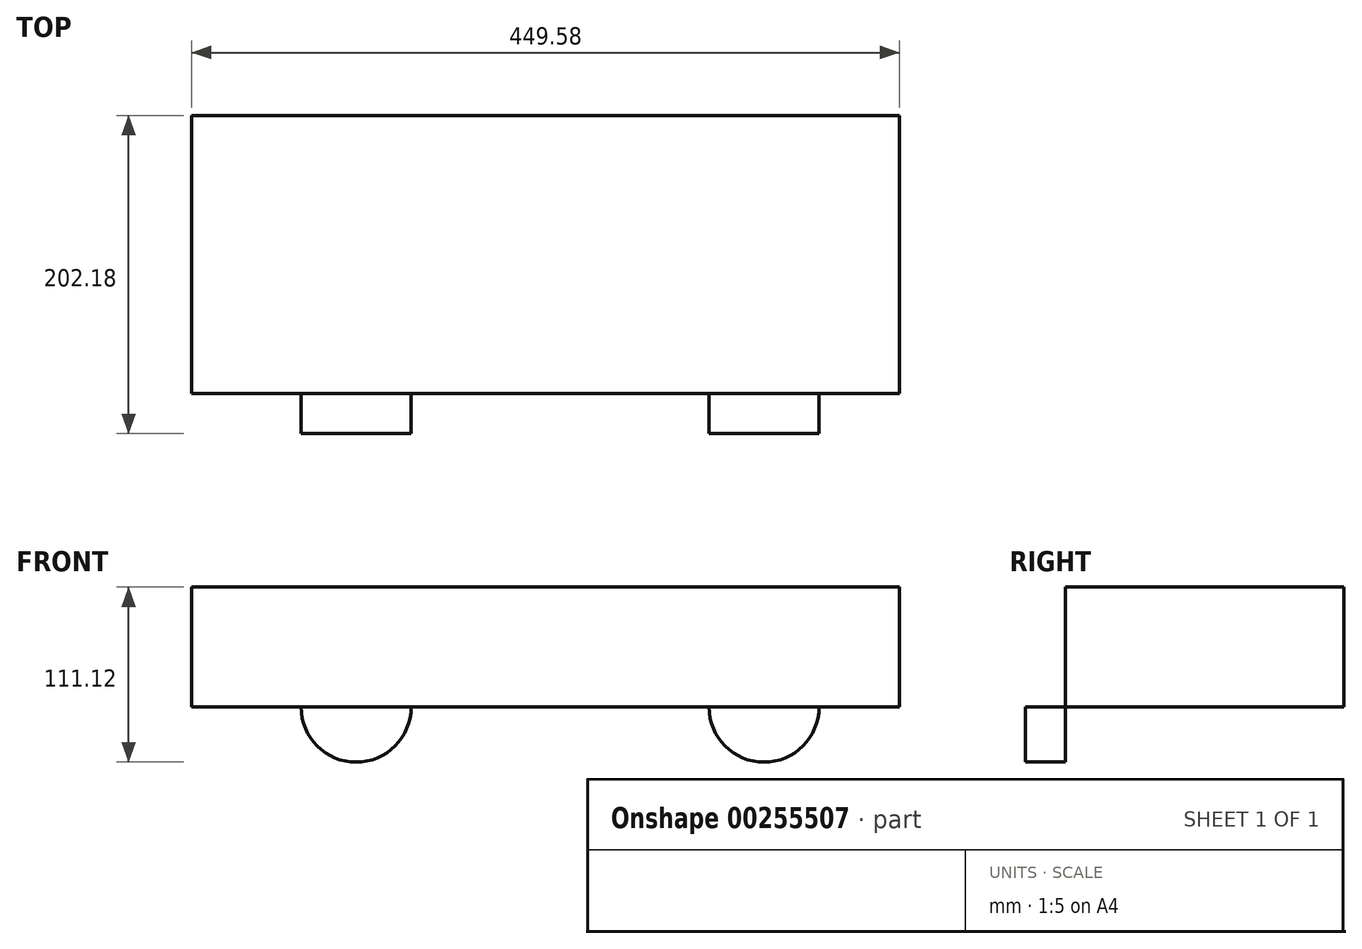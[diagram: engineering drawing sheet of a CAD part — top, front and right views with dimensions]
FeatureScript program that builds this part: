
annotation { "Feature Type Name" : "Feature", "Feature Type Description" : "" }
export const myFeature = defineFeature(function(context is Context, id is Id, definition is map)
    precondition{}
    {
        {
            var Q0;
            Q0=qCreatedBy(makeId("Top.planeOp"),FACE);
            var sketch = newSketch(context, id + "F0", { "sketchPlane" : qUnion([Q0])});
            skLineSegment(sketch, "E0.bottom", {"start": v(-126.41, 88.76) * mm, "end": v(323.17, 88.76) * mm});
            skLineSegment(sketch, "E0.top", {"start": v(-126.41, -88.02) * mm, "end": v(323.17, -88.02) * mm});
            skLineSegment(sketch, "E0.left", {"start": v(-126.41, 88.76) * mm, "end": v(-126.41, -88.02) * mm});
            skLineSegment(sketch, "E0.right", {"start": v(323.17, 88.76) * mm, "end": v(323.17, -88.02) * mm});
            skSolve(sketch);
        }
        {
            var Q0;
            Q0=makeQuery(id+"F0.imprint","IMPRINT",FACE,{"disambiguationData":[TD([[makeQuery(id+"F0.imprint","IMPRINT",EDGE,{"derivedFrom":sQuery(id+"F0.wireOp",EDGE,"E0.bottom")}),-1.0]])]});
            extrude(context, id + "F1", {"entities" : qUnion([Q0]), "depth" : 76.2 * mm});
        }
        {
            var Q0;
            Q0=makeQuery(id+"F1.opExtrude","SWEPT_FACE",FACE,{"disambiguationData":[OSD([sQuery(id+"F0.wireOp",EDGE,"E0.top")])]});
            var sketch = newSketch(context, id + "F2", { "sketchPlane" : qUnion([Q0])});
            skCircle(sketch, "E1", {"center": v(-21.95, 0) * mm, "radius": 34.93 * mm});
            skCircle(sketch, "E2", {"center": v(237.13, 0) * mm, "radius": 34.93 * mm});
            skSolve(sketch);
        }
        {
            var Q0;
            {var subQ0=sQuery(id+"F2.wireOp",EDGE,"E2");var subQ1=makeQuery(id+"F1.opExtrude","CAP_EDGE",EDGE,{"disambiguationData":[OSD([sQuery(id+"F0.wireOp",EDGE,"E0.top")])],"isStart":true});var subQ2=makeQuery(id+"F2.imprint","INTERSECT",VERTEX,{"disambiguationData":[OD(0.0)],"derivedFrom":[subQ1,subQ0]});Q0=makeQuery(id+"F2.imprint","IMPRINT",FACE,{"disambiguationData":[TD([[makeQuery(id+"F2.imprint","IMPRINT",EDGE,{"disambiguationData":[TD([[subQ2,1.0]])],"derivedFrom":subQ0}),1.0]])]});}
            var Q1;
            {var subQ0=sQuery(id+"F2.wireOp",EDGE,"E1");var subQ1=makeQuery(id+"F1.opExtrude","CAP_EDGE",EDGE,{"disambiguationData":[OSD([sQuery(id+"F0.wireOp",EDGE,"E0.top")])],"isStart":true});var subQ2=makeQuery(id+"F2.imprint","INTERSECT",VERTEX,{"disambiguationData":[OD(0.0)],"derivedFrom":[subQ1,subQ0]});Q1=makeQuery(id+"F2.imprint","IMPRINT",FACE,{"disambiguationData":[TD([[makeQuery(id+"F2.imprint","IMPRINT",EDGE,{"disambiguationData":[TD([[subQ2,-1.0]])],"derivedFrom":subQ0}),1.0]])]});}
            extrude(context, id + "F3", {"entities" : qUnion([Q0, Q1]), "depth" : 25.4 * mm});
        }
    });
